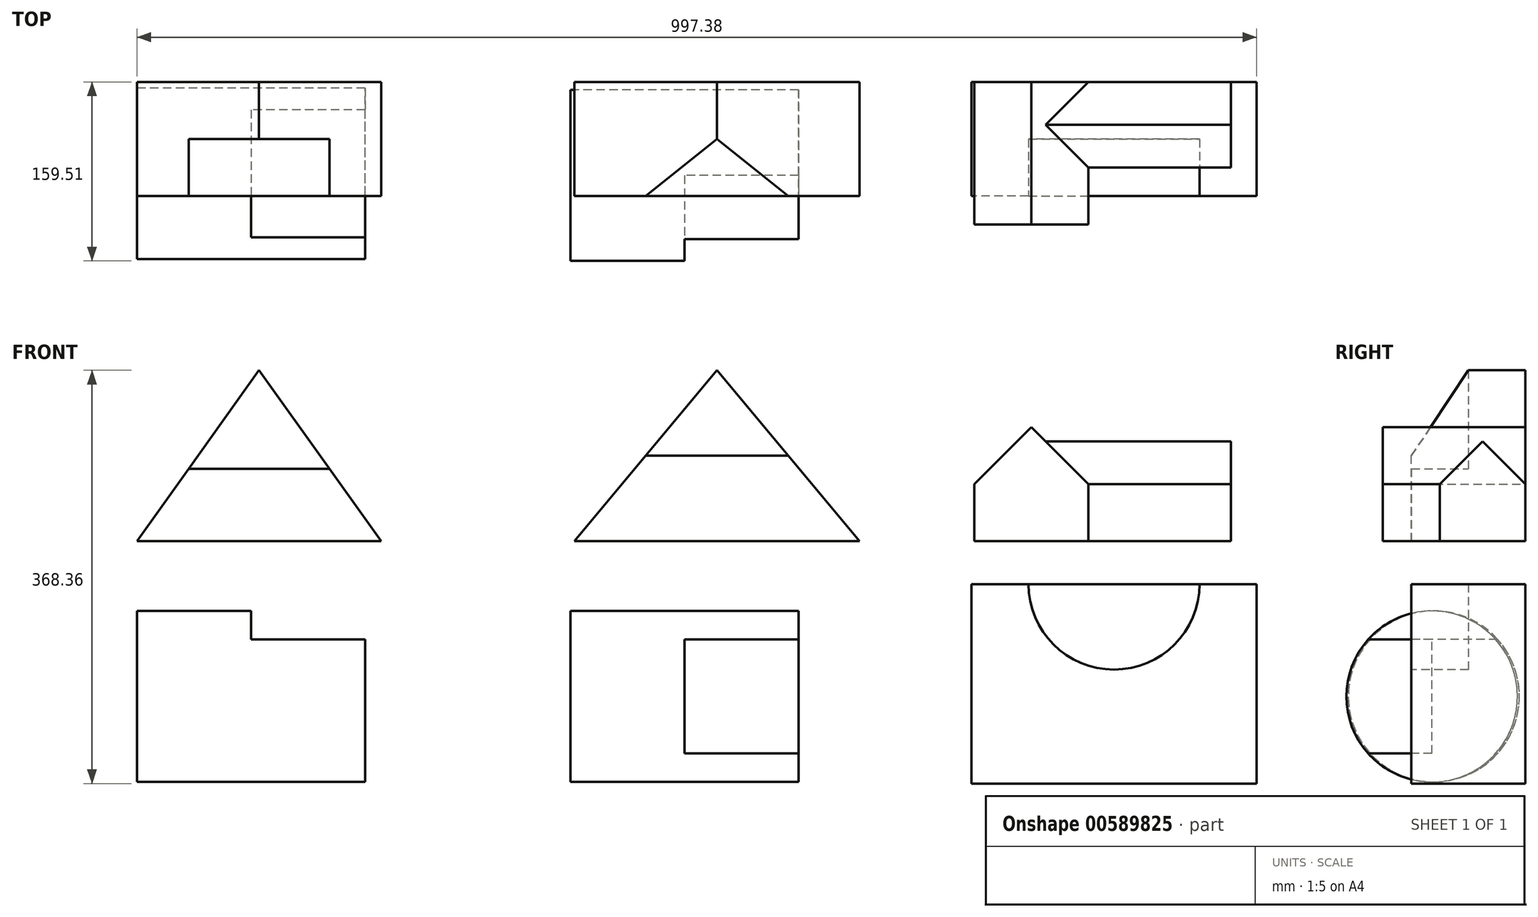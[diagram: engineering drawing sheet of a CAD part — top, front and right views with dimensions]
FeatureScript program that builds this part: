
annotation { "Feature Type Name" : "Feature", "Feature Type Description" : "" }
export const myFeature = defineFeature(function(context is Context, id is Id, definition is map)
    precondition{}
    {
        {
            var Q0;
            Q0=qCreatedBy(makeId("Front.planeOp"),FACE);
            var sketch = newSketch(context, id + "F0", { "sketchPlane" : qUnion([Q0])});
            skLineSegment(sketch, "E0", {"start": v(0, 0) * mm, "end": v(217.71, 0) * mm});
            skLineSegment(sketch, "E1", {"start": v(0, 0) * mm, "end": v(108.86, 152.4) * mm});
            skLineSegment(sketch, "E2", {"start": v(108.86, 152.4) * mm, "end": v(217.71, 0) * mm});
            skLineSegment(sketch, "E3", {"start": v(108.86, 64.71) * mm, "end": v(171.5, 64.71) * mm});
            skLineSegment(sketch, "E4", {"start": v(108.86, 64.71) * mm, "end": v(46.22, 64.71) * mm});
            skSolve(sketch);
        }
        {
            var Q0;
            {var subQ1=sQuery(id+"F0.wireOp",EDGE,"E0");Q0=makeQuery(id+"F0.imprint","IMPRINT",FACE,{"disambiguationData":[TD([[makeQuery(id+"F0.imprint","IMPRINT",EDGE,{"derivedFrom":subQ1}),1.0]])]});}
            extrude(context, id + "F1", {"entities" : qUnion([Q0]), "depth" : 101.6 * mm, "offsetDistance" : 25.4 * mm});
        }
        {
            var Q0;
            Q0 = qSketchRegion(id + "F0", true);
            extrude(context, id + "F2", {"entities" : qUnion([Q0]), "operationType" : NewBodyOperationType.ADD, "depth" : 50.8 * mm, "offsetDistance" : 25.4 * mm});
        }
        {
            var Q0;
            Q0=qCreatedBy(makeId("Front.planeOp"),FACE);
            var sketch = newSketch(context, id + "F3", { "sketchPlane" : qUnion([Q0])});
            skLineSegment(sketch, "E5", {"start": v(389.58, 0) * mm, "end": v(643.58, 0) * mm});
            skLineSegment(sketch, "E6", {"start": v(389.58, 0) * mm, "end": v(516.58, 152.4) * mm});
            skLineSegment(sketch, "E7", {"start": v(516.58, 152.4) * mm, "end": v(643.58, 0) * mm});
            skSolve(sketch);
        }
        {
            var Q0;
            Q0=makeQuery(id+"F3.imprint","IMPRINT",FACE,{"disambiguationData":[TD([[makeQuery(id+"F3.imprint","IMPRINT",EDGE,{"derivedFrom":sQuery(id+"F3.wireOp",EDGE,"E5")}),1.0]])]});
            extrude(context, id + "F4", {"entities" : qUnion([Q0]), "depth" : 101.6 * mm, "offsetDistance" : 25.4 * mm});
        }
        {
            var Q0;
            Q0=makeQuery(id+"F4.opExtrude","CAP_EDGE",EDGE,{"disambiguationData":[OSD([sQuery(id+"F3.wireOp",EDGE,"E5")])],"isStart":false});
            cPoint(context, id + "F5", {"entities" : qUnion([Q0]), "parameter" : 0.5});
        }
        {
            var Q0;
            Q0=makeQuery(id+"F4.opExtrude","CAP_VERTEX",VERTEX,{"disambiguationData":[OSD([sQuery(id+"F3.wireOp",EDGE,"E6"),sQuery(id+"F3.wireOp",EDGE,"E7")])],"isStart":false});
            var Q1;
            Q1=makeQuery(id+"F4.opExtrude","CAP_VERTEX",VERTEX,{"disambiguationData":[OSD([sQuery(id+"F3.wireOp",EDGE,"E6"),sQuery(id+"F3.wireOp",EDGE,"E7")])],"isStart":true});
            var Q2;
            Q2 = qCreatedBy(id + "F5" ,VERTEX);
            cPlane(context, id + "F6", {"entities" : qUnion([Q0, Q1, Q2]), "cplaneType" : CPlaneType.THREE_POINT, "offset" : 25.4 * mm, "width" : 152.4 * mm, "height" : 152.4 * mm});
        }
        {
            var Q0;
            Q0=qCreatedBy(id+"F6.planeOp",FACE);
            var sketch = newSketch(context, id + "F7", { "sketchPlane" : qUnion([Q0])});
            skPoint(sketch, "E8.0", {"position": v(-101.6, 152.4) * mm});
            skPoint(sketch, "E9.0", {"position": v(0, 152.4) * mm});
            skLineSegment(sketch, "E10.0", {"start": v(-101.6, 152.4) * mm, "end": v(0, 152.4) * mm});
            skLineSegment(sketch, "E11", {"start": v(-101.6, 152.4) * mm, "end": v(-50.8, 152.4) * mm});
            skLineSegment(sketch, "E12", {"start": v(-50.8, 152.4) * mm, "end": v(-101.6, 76.2) * mm});
            skLineSegment(sketch, "E13", {"start": v(-101.6, 76.2) * mm, "end": v(-101.6, 152.4) * mm});
            skSolve(sketch);
        }
        {
            var Q0;
            Q0 = qSketchRegion(id + "F7", true);
            extrude(context, id + "F8", {"entities" : qUnion([Q0]), "operationType" : NewBodyOperationType.REMOVE, "endBound" : BoundingType.SYMMETRIC, "oppositeDirection" : true, "depth" : 152.4 * mm, "offsetDistance" : 25.4 * mm});
        }
        {
            var Q0;
            Q0=qCreatedBy(makeId("Front.planeOp"),FACE);
            var sketch = newSketch(context, id + "F9", { "sketchPlane" : qUnion([Q0])});
            skLineSegment(sketch, "E14", {"start": v(745.83, 0) * mm, "end": v(974.43, 0) * mm});
            skLineSegment(sketch, "E15", {"start": v(974.43, 0) * mm, "end": v(974.43, 88.9) * mm});
            skLineSegment(sketch, "E16", {"start": v(745.83, 0) * mm, "end": v(745.83, 50.8) * mm});
            skLineSegment(sketch, "E17", {"start": v(847.59, 50.8) * mm, "end": v(847.59, 0) * mm});
            skLineSegment(sketch, "E18", {"start": v(847.59, 50.8) * mm, "end": v(974.43, 50.8) * mm});
            skLineSegment(sketch, "E19", {"start": v(974.43, 88.9) * mm, "end": v(809.33, 88.9) * mm});
            skLineSegment(sketch, "E20", {"start": v(847.59, 50.8) * mm, "end": v(796.63, 101.6) * mm});
            skLineSegment(sketch, "E21", {"start": v(796.63, 101.6) * mm, "end": v(745.83, 50.8) * mm});
            skSolve(sketch);
        }
        {
            var Q0;
            {var subQ3=sQuery(id+"F9.wireOp",EDGE,"E16");Q0=makeQuery(id+"F9.imprint","IMPRINT",FACE,{"disambiguationData":[TD([[makeQuery(id+"F9.imprint","IMPRINT",EDGE,{"derivedFrom":subQ3}),-1.0]])]});}
            extrude(context, id + "F10", {"entities" : qUnion([Q0]), "depth" : 127 * mm, "offsetDistance" : 25.4 * mm});
        }
        {
            var Q0;
            {var subQ3=sQuery(id+"F9.wireOp",EDGE,"E17");Q0=makeQuery(id+"F9.imprint","IMPRINT",FACE,{"disambiguationData":[TD([[makeQuery(id+"F9.imprint","IMPRINT",EDGE,{"derivedFrom":subQ3}),1.0]])]});}
            extrude(context, id + "F11", {"entities" : qUnion([Q0]), "operationType" : NewBodyOperationType.ADD, "depth" : 76.2 * mm, "offsetDistance" : 25.4 * mm});
        }
        {
            var Q0;
            Q0=makeQuery(id+"F11.opExtrude","SWEPT_FACE",FACE,{"disambiguationData":[OSD([sQuery(id+"F9.wireOp",EDGE,"E15")])]});
            var sketch = newSketch(context, id + "F12", { "sketchPlane" : qUnion([Q0])});
            skPoint(sketch, "E22.endSnap0", {"position": v(-38.1, 50.8) * mm});
            skLineSegment(sketch, "E23", {"start": v(-76.2, 50.8) * mm, "end": v(-38.1, 88.9) * mm});
            skLineSegment(sketch, "E24", {"start": v(0, 50.8) * mm, "end": v(-38.1, 88.9) * mm});
            skSolve(sketch);
        }
        {
            var Q0;
            Q0=makeQuery(id+"F12.imprint","IMPRINT",FACE,{"disambiguationData":[TD([[makeQuery(id+"F12.imprint","IMPRINT",EDGE,{"derivedFrom":sQuery(id+"F12.wireOp",EDGE,"E23")}),-1.0]])]});
            extrude(context, id + "F13", {"entities" : qUnion([Q0]), "operationType" : NewBodyOperationType.ADD, "endBound" : BoundingType.UP_TO_NEXT, "oppositeDirection" : true, "depth" : 25.4 * mm, "offsetDistance" : 25.4 * mm});
        }
        {
            var Q0;
            Q0=qCreatedBy(makeId("Right.planeOp"),FACE);
            var sketch = newSketch(context, id + "F14", { "sketchPlane" : qUnion([Q0])});
            skCircle(sketch, "E25", {"center": v(-81.63, -138.28) * mm, "radius": 76.2 * mm});
            skLineSegment(sketch, "E26", {"start": v(-81.63, -87.48) * mm, "end": v(-24.83, -87.48) * mm});
            skLineSegment(sketch, "E27", {"start": v(-81.63, -87.48) * mm, "end": v(-138.42, -87.48) * mm});
            skSolve(sketch);
        }
        {
            var Q0;
            {var subQ0=sQuery(id+"F14.wireOp",EDGE,"E26");Q0=makeQuery(id+"F14.imprint","IMPRINT",FACE,{"disambiguationData":[TD([[makeQuery(id+"F14.imprint","IMPRINT",EDGE,{"derivedFrom":subQ0}),-1.0]])]});}
            extrude(context, id + "F15", {"entities" : qUnion([Q0]), "depth" : 203.2 * mm, "offsetDistance" : 25.4 * mm});
        }
        {
            var Q0;
            {var subQ0=sQuery(id+"F14.wireOp",EDGE,"E26");Q0=makeQuery(id+"F14.imprint","IMPRINT",FACE,{"disambiguationData":[TD([[makeQuery(id+"F14.imprint","IMPRINT",EDGE,{"derivedFrom":subQ0}),1.0]])]});}
            extrude(context, id + "F16", {"entities" : qUnion([Q0]), "operationType" : NewBodyOperationType.ADD, "depth" : 101.6 * mm, "offsetDistance" : 25.4 * mm});
        }
        {
            var Q0;
            Q0=qCreatedBy(makeId("Right.planeOp"),FACE);
            cPlane(context, id + "F17", {"entities" : qUnion([Q0]), "cplaneType" : CPlaneType.OFFSET, "offset" : 386.08 * mm, "width" : 152.4 * mm, "height" : 152.4 * mm});
        }
        {
            var Q0;
            Q0=qCreatedBy(id+"F17.planeOp",FACE);
            var sketch = newSketch(context, id + "F18", { "sketchPlane" : qUnion([Q0])});
            skCircle(sketch, "E28", {"center": v(-83.3, -138.35) * mm, "radius": 76.2 * mm});
            skLineSegment(sketch, "E29", {"start": v(-83.3, -189.15) * mm, "end": v(-140.1, -189.15) * mm});
            skLineSegment(sketch, "E30", {"start": v(-83.3, -189.15) * mm, "end": v(-83.3, -87.55) * mm});
            skLineSegment(sketch, "E31", {"start": v(-83.3, -87.55) * mm, "end": v(-140.1, -87.55) * mm});
            skSolve(sketch);
        }
        {
            var Q0;
            {var subQ0=sQuery(id+"F18.wireOp",EDGE,"E29");Q0=makeQuery(id+"F18.imprint","IMPRINT",FACE,{"disambiguationData":[TD([[makeQuery(id+"F18.imprint","IMPRINT",EDGE,{"derivedFrom":subQ0}),1.0]])]});}
            extrude(context, id + "F19", {"entities" : qUnion([Q0]), "depth" : 203.2 * mm, "offsetDistance" : 25.4 * mm});
        }
        {
            var Q0;
            {var subQ0=sQuery(id+"F18.wireOp",EDGE,"E29");Q0=makeQuery(id+"F18.imprint","IMPRINT",FACE,{"disambiguationData":[TD([[makeQuery(id+"F18.imprint","IMPRINT",EDGE,{"derivedFrom":subQ0}),-1.0]])]});}
            extrude(context, id + "F20", {"entities" : qUnion([Q0]), "operationType" : NewBodyOperationType.ADD, "depth" : 101.6 * mm, "offsetDistance" : 25.4 * mm});
        }
        {
            var Q0;
            Q0=qCreatedBy(makeId("Front.planeOp"),FACE);
            var sketch = newSketch(context, id + "F21", { "sketchPlane" : qUnion([Q0])});
            skLineSegment(sketch, "E32", {"start": v(743.38, -215.96) * mm, "end": v(997.38, -215.96) * mm});
            skLineSegment(sketch, "E33", {"start": v(997.38, -215.96) * mm, "end": v(997.38, -38.16) * mm});
            skLineSegment(sketch, "E34", {"start": v(997.38, -38.16) * mm, "end": v(743.38, -38.16) * mm});
            skLineSegment(sketch, "E35", {"start": v(743.38, -38.16) * mm, "end": v(743.38, -215.96) * mm});
            skArc(sketch, "E36", {"start": v(794.18, -38.16) * mm, "mid": v(870.38, -114.36) * mm, "end": v(946.58, -38.16) * mm});
            skSolve(sketch);
        }
        {
            var Q0;
            {var subQ0=sQuery(id+"F21.wireOp",EDGE,"E36");Q0=makeQuery(id+"F21.imprint","IMPRINT",FACE,{"disambiguationData":[TD([[makeQuery(id+"F21.imprint","IMPRINT",EDGE,{"derivedFrom":subQ0}),1.0]])]});}
            var Q1;
            Q1=makeQuery(id+"F21.imprint","IMPRINT",FACE,{"disambiguationData":[TD([[makeQuery(id+"F21.imprint","IMPRINT",EDGE,{"derivedFrom":sQuery(id+"F21.wireOp",EDGE,"E32")}),1.0]])]});
            extrude(context, id + "F22", {"entities" : qUnion([Q0, Q1]), "depth" : 101.6 * mm, "offsetDistance" : 25.4 * mm});
        }
        {
            var Q0;
            Q0=makeQuery(id+"F22.opExtrude","CAP_FACE",FACE,{"disambiguationData":[OSD([sQuery(id+"F21.wireOp",EDGE,"E32"),sQuery(id+"F21.wireOp",EDGE,"E33"),sQuery(id+"F21.wireOp",EDGE,"E34"),sQuery(id+"F21.wireOp",EDGE,"E35")])],"isStart":false});
            var sketch = newSketch(context, id + "F23", { "sketchPlane" : qUnion([Q0])});
            skLineSegment(sketch, "E37", {"start": v(743.38, -38.16) * mm, "end": v(794.18, -38.16) * mm});
            skLineSegment(sketch, "E38", {"start": v(997.38, -38.16) * mm, "end": v(946.58, -38.16) * mm});
            skArc(sketch, "E39", {"start": v(794.18, -38.16) * mm, "mid": v(870.38, -114.36) * mm, "end": v(946.58, -38.16) * mm});
            skSolve(sketch);
        }
        {
            var Q0;
            {var subQ0=sQuery(id+"F23.wireOp",EDGE,"E39");Q0=makeQuery(id+"F23.imprint","IMPRINT",FACE,{"disambiguationData":[TD([[makeQuery(id+"F23.imprint","IMPRINT",EDGE,{"derivedFrom":subQ0}),1.0]])]});}
            extrude(context, id + "F24", {"entities" : qUnion([Q0]), "operationType" : NewBodyOperationType.REMOVE, "oppositeDirection" : true, "depth" : 50.8 * mm, "offsetDistance" : 25.4 * mm});
        }
    });
